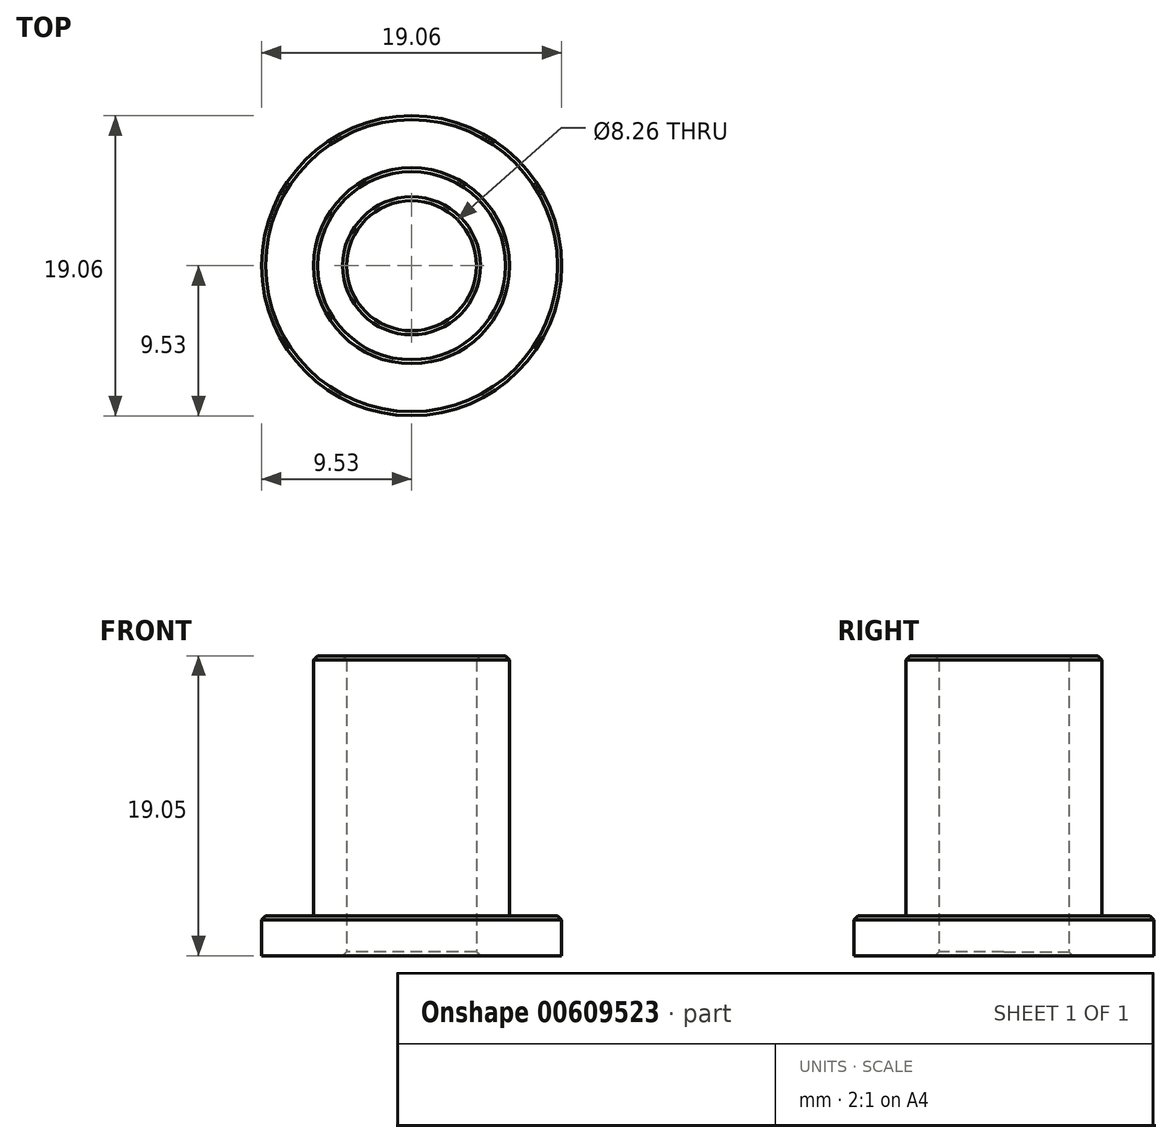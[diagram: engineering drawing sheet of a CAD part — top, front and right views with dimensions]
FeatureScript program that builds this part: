
annotation { "Feature Type Name" : "Feature", "Feature Type Description" : "" }
export const myFeature = defineFeature(function(context is Context, id is Id, definition is map)
    precondition{}
    {
        {
            var Q0;
            Q0=qCreatedBy(makeId("Front.planeOp"),FACE);
            var sketch = newSketch(context, id + "F0", { "sketchPlane" : qUnion([Q0])});
            skLineSegment(sketch, "E0", {"start": v(0, 0) * mm, "end": v(0, 16.54) * mm, "construction": true});
            skLineSegment(sketch, "E1", {"start": v(4.13, 0) * mm, "end": v(4.13, 19.05) * mm});
            skLineSegment(sketch, "E2", {"start": v(4.13, 19.05) * mm, "end": v(6.22, 19.05) * mm});
            skLineSegment(sketch, "E3", {"start": v(6.22, 19.05) * mm, "end": v(6.22, 2.54) * mm});
            skLineSegment(sketch, "E4", {"start": v(6.22, 2.54) * mm, "end": v(9.53, 2.54) * mm});
            skLineSegment(sketch, "E5", {"start": v(9.53, 2.54) * mm, "end": v(9.53, 0) * mm});
            skLineSegment(sketch, "E6", {"start": v(9.53, 0) * mm, "end": v(4.13, 0) * mm});
            skSolve(sketch);
        }
        {
            var Q0;
            Q0=qSketchRegion(id+"F0",true);
            var Q1;
            Q1=sQuery(id+"F0.wireOp",EDGE,"E0");
            revolve(context, id + "F1", {"entities" : qUnion([Q0]), "axis" : qUnion([Q1]), "revolveType" : RevolveType.FULL});
        }
        {
            var Q0;
            Q0=makeQuery(id+"F1.opRevolve","SWEPT_EDGE",EDGE,{"disambiguationData":[OSD([sQuery(id+"F0.wireOp",EDGE,"E2"),sQuery(id+"F0.wireOp",EDGE,"E3")])]});
            var Q1;
            Q1=makeQuery(id+"F1.opRevolve","SWEPT_FACE",FACE,{"disambiguationData":[OSD([sQuery(id+"F0.wireOp",EDGE,"E2")])]});
            var Q2;
            Q2=makeQuery(id+"F1.opRevolve","SWEPT_EDGE",EDGE,{"disambiguationData":[OSD([sQuery(id+"F0.wireOp",EDGE,"E4"),sQuery(id+"F0.wireOp",EDGE,"E5")])]});
            var Q3;
            Q3=makeQuery(id+"F1.opRevolve","SWEPT_EDGE",EDGE,{"disambiguationData":[OSD([sQuery(id+"F0.wireOp",EDGE,"E1"),sQuery(id+"F0.wireOp",EDGE,"E6")])]});
            chamfer(context, id + "F2", {"entities" : qUnion([Q0, Q1, Q2, Q3]), "width" : 0.25 * mm, "tangentPropagation" : true});
        }
    });
